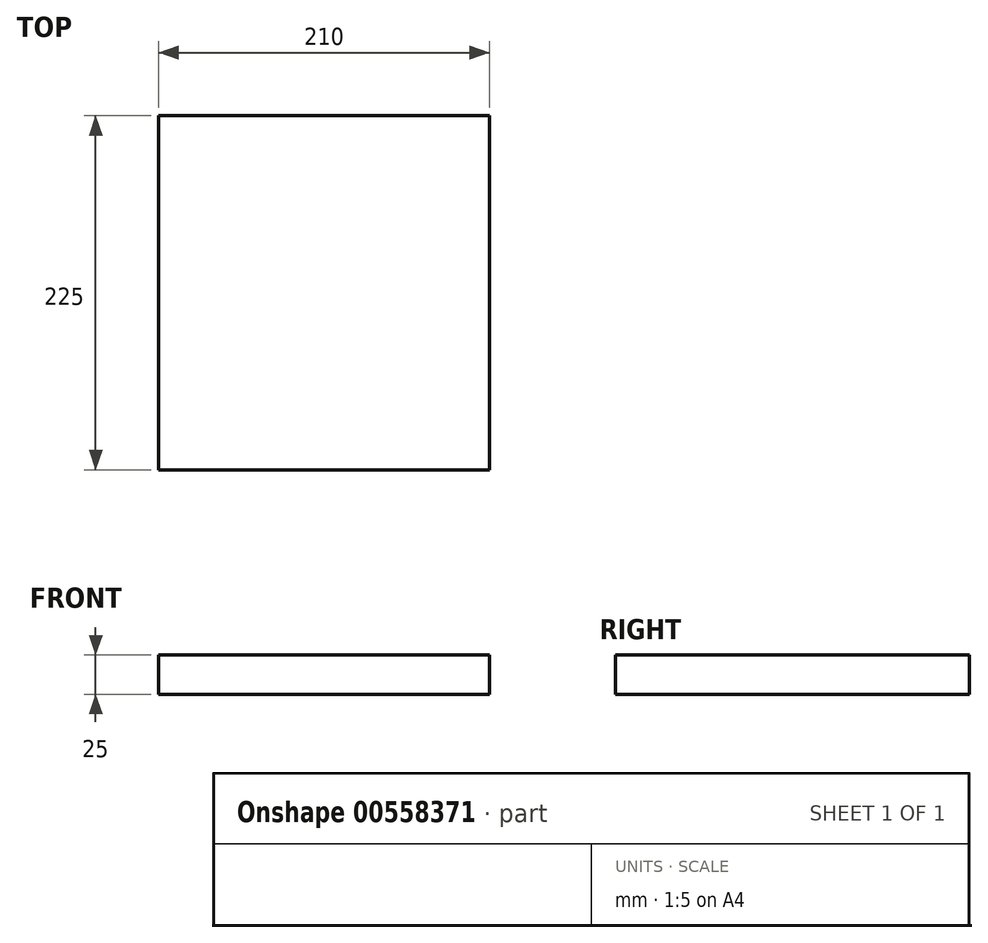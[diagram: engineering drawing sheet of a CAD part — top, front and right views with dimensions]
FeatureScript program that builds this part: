
annotation { "Feature Type Name" : "Feature", "Feature Type Description" : "" }
export const myFeature = defineFeature(function(context is Context, id is Id, definition is map)
    precondition{}
    {
        {
            var Q0;
            Q0=qCreatedBy(makeId("Top.planeOp"),FACE);
            var sketch = newSketch(context, id + "F0", { "sketchPlane" : qUnion([Q0])});
            skLineSegment(sketch, "E0.bottom", {"start": v(-95.7, -112.1) * mm, "end": v(114.3, -112.1) * mm});
            skLineSegment(sketch, "E0.top", {"start": v(-95.7, 112.9) * mm, "end": v(114.3, 112.9) * mm});
            skLineSegment(sketch, "E0.left", {"start": v(-95.7, -112.1) * mm, "end": v(-95.7, 112.9) * mm});
            skLineSegment(sketch, "E0.right", {"start": v(114.3, -112.1) * mm, "end": v(114.3, 112.9) * mm});
            skPoint(sketch, "E1", {"position": v(-40.43, -112.1) * mm});
            skPoint(sketch, "E2", {"position": v(45.5, -112.1) * mm});
            skPoint(sketch, "E3", {"position": v(-64.73, -112.1) * mm});
            skPoint(sketch, "E4", {"position": v(114.3, 92.23) * mm});
            skPoint(sketch, "E5", {"position": v(114.3, 46.38) * mm});
            skPoint(sketch, "E6", {"position": v(114.3, 0.4) * mm});
            skSolve(sketch);
        }
        {
            var Q0;
            Q0 = qSketchRegion(id + "F0", true);
            var Q1;
            Q1 = qSketchRegion(id + "F2", true);
            extrude(context, id + "F1", {"entities" : qUnion([Q0, Q1]), "endBound" : BoundingType.SYMMETRIC, "depth" : 25 * mm, "offsetDistance" : 25 * mm});
        }
    });
